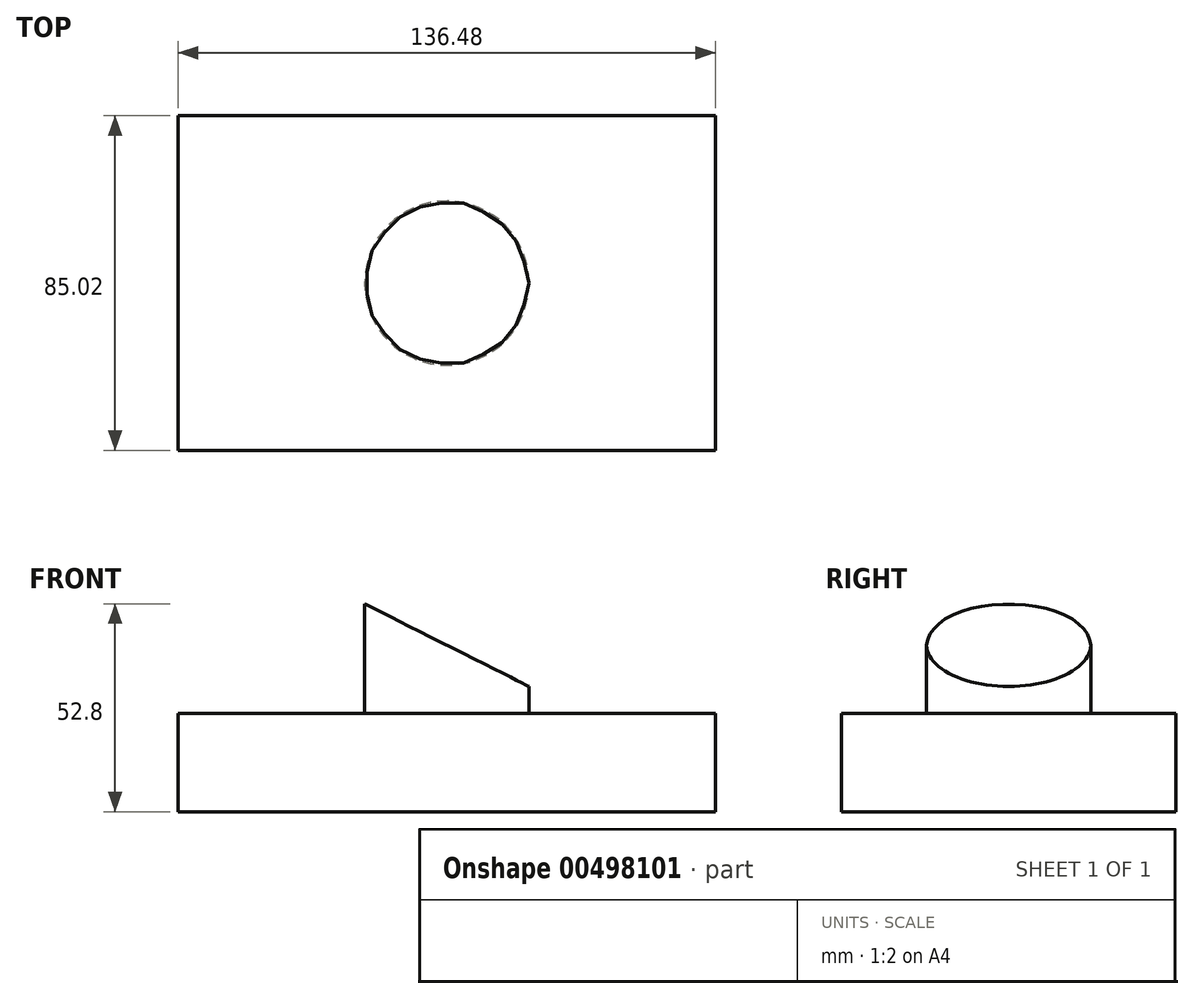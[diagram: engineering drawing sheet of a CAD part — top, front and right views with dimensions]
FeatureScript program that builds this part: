
annotation { "Feature Type Name" : "Feature", "Feature Type Description" : "" }
export const myFeature = defineFeature(function(context is Context, id is Id, definition is map)
    precondition{}
    {
        {
            var Q0;
            Q0=qCreatedBy(makeId("Top.planeOp"),FACE);
            var sketch = newSketch(context, id + "F0", { "sketchPlane" : qUnion([Q0])});
            skLineSegment(sketch, "E0.bottom", {"start": v(68.24, 42.5) * mm, "end": v(-68.24, 42.5) * mm});
            skLineSegment(sketch, "E0.top", {"start": v(68.24, -42.5) * mm, "end": v(-68.24, -42.5) * mm});
            skLineSegment(sketch, "E0.left", {"start": v(68.24, 42.5) * mm, "end": v(68.24, -42.5) * mm});
            skLineSegment(sketch, "E0.right", {"start": v(-68.24, 42.5) * mm, "end": v(-68.24, -42.5) * mm});
            skPoint(sketch, "E0.middle", {"position": v(0, 0) * mm});
            skCircle(sketch, "E1", {"center": v(0, 0) * mm, "radius": 20.85 * mm});
            skSolve(sketch);
        }
        {
            var Q0;
            Q0 = qSketchRegion(id + "F0", true);
            extrude(context, id + "F1", {"entities" : qUnion([Q0]), "depth" : 25 * mm});
        }
        {
            var Q0;
            Q0=makeQuery(id+"F0.imprint","IMPRINT",FACE,{"disambiguationData":[TD([[makeQuery(id+"F0.imprint","IMPRINT",EDGE,{"derivedFrom":sQuery(id+"F0.wireOp",EDGE,"E1")}),1.0]])]});
            extrude(context, id + "F2", {"entities" : qUnion([Q0]), "operationType" : NewBodyOperationType.ADD, "depth" : 52.8 * mm});
        }
        {
            var Q0;
            Q0=qCreatedBy(makeId("Front.planeOp"),FACE);
            var sketch = newSketch(context, id + "F3", { "sketchPlane" : qUnion([Q0])});
            skLineSegment(sketch, "E2.0", {"start": v(-20.85, 52.8) * mm, "end": v(20.85, 52.8) * mm});
            skLineSegment(sketch, "E3", {"start": v(20.85, 52.8) * mm, "end": v(20.85, 25) * mm});
            skLineSegment(sketch, "E4", {"start": v(-20.85, 25) * mm, "end": v(-20.85, 52.8) * mm});
            skLineSegment(sketch, "E5", {"start": v(-20.85, 52.8) * mm, "end": v(20.85, 31.84) * mm});
            skSolve(sketch);
        }
        {
            var Q0;
            Q0 = qSketchRegion(id + "F3", true);
            extrude(context, id + "F4", {"entities" : qUnion([Q0]), "operationType" : NewBodyOperationType.REMOVE, "endBound" : BoundingType.SYMMETRIC, "depth" : 95.2 * mm});
        }
    });
